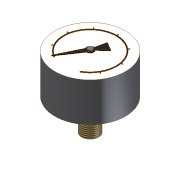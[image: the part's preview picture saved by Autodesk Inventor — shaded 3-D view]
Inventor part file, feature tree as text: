
AUTODESK INVENTOR PART (.ipt)
format: ipt  version: unknown  size: 241,664 bytes
history: native  units: mm
features: imported_body x1, thread x1
ambient origin geometry x8: Origin, YZ Plane, XZ Plane, XY Plane, X Axis, Y Axis, Z Axis, Center Point
feature tree (2):
  imported_body  "Base1"
  thread  "Thread1"  [1 undecoded]
note: 1 required parameter value undecoded (feature->parameter linkage not recoverable at this tier; creation-order binding heuristic only, values carry confidence <= 0.55)
